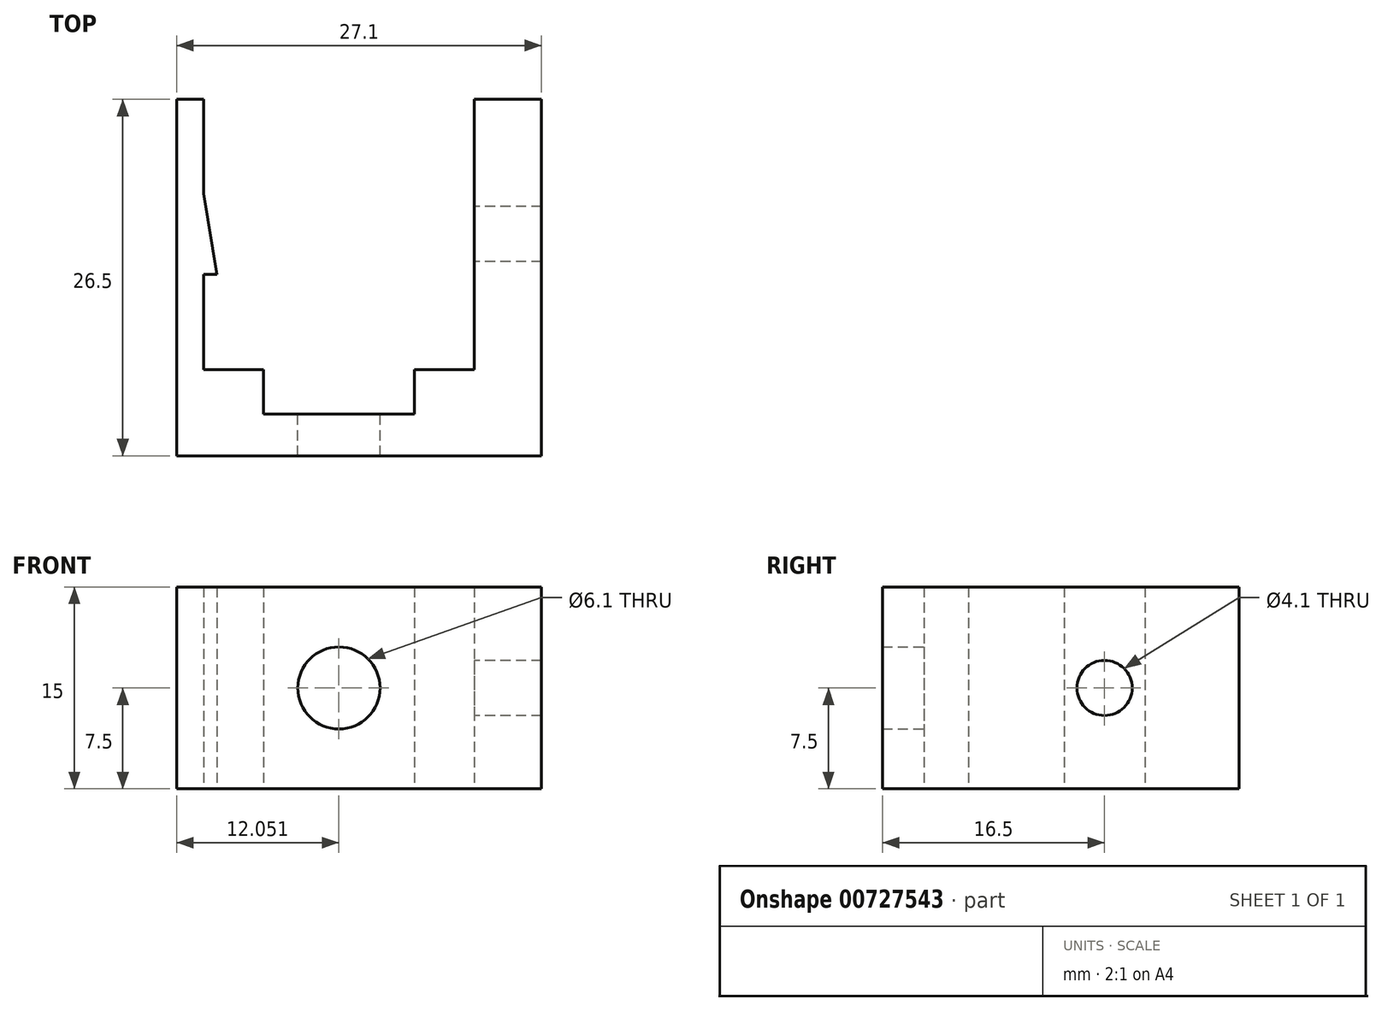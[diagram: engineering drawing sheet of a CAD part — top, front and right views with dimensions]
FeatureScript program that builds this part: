
annotation { "Feature Type Name" : "Feature", "Feature Type Description" : "" }
export const myFeature = defineFeature(function(context is Context, id is Id, definition is map)
    precondition{}
    {
        {
            var Q0;
            Q0=qCreatedBy(makeId("Top.planeOp"),FACE);
            var sketch = newSketch(context, id + "F0", { "sketchPlane" : qUnion([Q0])});
            skLineSegment(sketch, "E0", {"start": v(-10.68, 13) * mm, "end": v(-8.68, 13) * mm});
            skLineSegment(sketch, "E1", {"start": v(-8.68, 13) * mm, "end": v(-8.68, 6) * mm});
            skLineSegment(sketch, "E2", {"start": v(-8.68, 6) * mm, "end": v(-7.68, 0) * mm});
            skLineSegment(sketch, "E3", {"start": v(-7.68, 0) * mm, "end": v(-8.68, 0) * mm});
            skLineSegment(sketch, "E4", {"start": v(-8.68, 0) * mm, "end": v(-8.68, -7.1) * mm});
            skLineSegment(sketch, "E5", {"start": v(-8.68, -7.1) * mm, "end": v(-4.23, -7.1) * mm});
            skLineSegment(sketch, "E6", {"start": v(-4.23, -7.1) * mm, "end": v(-4.23, -10.4) * mm});
            skLineSegment(sketch, "E7", {"start": v(-4.23, -10.4) * mm, "end": v(6.97, -10.4) * mm});
            skLineSegment(sketch, "E8", {"start": v(6.97, -10.4) * mm, "end": v(6.97, -7.1) * mm});
            skLineSegment(sketch, "E9", {"start": v(6.97, -7.1) * mm, "end": v(11.42, -7.1) * mm});
            skLineSegment(sketch, "E10", {"start": v(11.42, 13) * mm, "end": v(16.42, 13) * mm});
            skLineSegment(sketch, "E11", {"start": v(16.42, 13) * mm, "end": v(16.42, -13.5) * mm});
            skLineSegment(sketch, "E12", {"start": v(16.42, -13.5) * mm, "end": v(-10.68, -13.5) * mm});
            skLineSegment(sketch, "E13", {"start": v(11.42, -7.1) * mm, "end": v(11.42, 13) * mm});
            skLineSegment(sketch, "E14", {"start": v(-10.68, 13) * mm, "end": v(-10.68, -13.5) * mm});
            skSolve(sketch);
        }
        {
            var Q0;
            Q0=makeQuery(id+"F0.imprint","IMPRINT",FACE,{"disambiguationData":[TD([[makeQuery(id+"F0.imprint","IMPRINT",EDGE,{"derivedFrom":sQuery(id+"F0.wireOp",EDGE,"E0")}),-1.0]])]});
            extrude(context, id + "F1", {"entities" : qUnion([Q0]), "depth" : 15 * mm, "offsetDistance" : 25 * mm});
        }
        {
            var Q0;
            Q0=makeQuery(id+"F1.opExtrude","SWEPT_FACE",FACE,{"disambiguationData":[OSD([sQuery(id+"F0.wireOp",EDGE,"E12")])]});
            var sketch = newSketch(context, id + "F2", { "sketchPlane" : qUnion([Q0])});
            skLineSegment(sketch, "E15", {"start": v(-4.23, 15) * mm, "end": v(6.97, 0) * mm, "construction": true});
            skPoint(sketch, "E16", {"position": v(1.37, 7.5) * mm});
            skLineSegment(sketch, "E17.0.0", {"start": v(6.97, 0) * mm, "end": v(-4.23, 0) * mm});
            skLineSegment(sketch, "E17.0.1", {"start": v(-4.23, 0) * mm, "end": v(-4.23, 15) * mm});
            skLineSegment(sketch, "E17.0.2", {"start": v(-4.23, 15) * mm, "end": v(6.97, 15) * mm});
            skLineSegment(sketch, "E17.0.3", {"start": v(6.97, 15) * mm, "end": v(6.97, 0) * mm});
            skSolve(sketch);
        }
        {
            var Q0;
            Q0=makeQuery(id+"F1.opExtrude","SWEPT_FACE",FACE,{"disambiguationData":[OSD([sQuery(id+"F0.wireOp",EDGE,"E11")])]});
            var sketch = newSketch(context, id + "F3", { "sketchPlane" : qUnion([Q0])});
            skLineSegment(sketch, "E18", {"start": v(13, 7.5) * mm, "end": v(-13.5, 7.5) * mm, "construction": true});
            skPoint(sketch, "E19", {"position": v(3, 7.5) * mm});
            skSolve(sketch);
        }
        {
            var Q0;
            Q0=sQuery(id+"F3.wireOp",VERTEX,"E19");
            var Q1;
            Q1=makeQuery(id+"F1.opExtrude","SWEPT_BODY",BODY,{"disambiguationData":[OSD([sQuery(id+"F0.wireOp",EDGE,"E0"),sQuery(id+"F0.wireOp",EDGE,"E1"),sQuery(id+"F0.wireOp",EDGE,"E2"),sQuery(id+"F0.wireOp",EDGE,"E3"),sQuery(id+"F0.wireOp",EDGE,"E4"),sQuery(id+"F0.wireOp",EDGE,"E5"),sQuery(id+"F0.wireOp",EDGE,"E6"),sQuery(id+"F0.wireOp",EDGE,"E7"),sQuery(id+"F0.wireOp",EDGE,"E8"),sQuery(id+"F0.wireOp",EDGE,"E9"),sQuery(id+"F0.wireOp",EDGE,"E10"),sQuery(id+"F0.wireOp",EDGE,"E11"),sQuery(id+"F0.wireOp",EDGE,"E12"),sQuery(id+"F0.wireOp",EDGE,"E13"),sQuery(id+"F0.wireOp",EDGE,"E14")])]});
            hole(context, id + "F4", {"style" : HoleStyle.SIMPLE, "endStyle" : HoleEndStyle.BLIND, "holeDiameter" : 4.1 * mm, "majorDiameter" : 20 * mm, "holeDepth" : 7 * mm, "tappedDepth" : 30 * mm, "tapClearance" : 3, "startFromSketch" : true, "locations" : qUnion([Q0]), "scope" : qUnion([Q1])});
        }
        {
            var Q0;
            Q0=sQuery(id+"F2.wireOp",VERTEX,"E16");
            var Q1;
            Q1=makeQuery(id+"F1.opExtrude","SWEPT_BODY",BODY,{"disambiguationData":[OSD([sQuery(id+"F0.wireOp",EDGE,"E0"),sQuery(id+"F0.wireOp",EDGE,"E1"),sQuery(id+"F0.wireOp",EDGE,"E2"),sQuery(id+"F0.wireOp",EDGE,"E3"),sQuery(id+"F0.wireOp",EDGE,"E4"),sQuery(id+"F0.wireOp",EDGE,"E5"),sQuery(id+"F0.wireOp",EDGE,"E6"),sQuery(id+"F0.wireOp",EDGE,"E7"),sQuery(id+"F0.wireOp",EDGE,"E8"),sQuery(id+"F0.wireOp",EDGE,"E9"),sQuery(id+"F0.wireOp",EDGE,"E10"),sQuery(id+"F0.wireOp",EDGE,"E11"),sQuery(id+"F0.wireOp",EDGE,"E12"),sQuery(id+"F0.wireOp",EDGE,"E13"),sQuery(id+"F0.wireOp",EDGE,"E14")])]});
            hole(context, id + "F5", {"style" : HoleStyle.SIMPLE, "endStyle" : HoleEndStyle.BLIND, "holeDiameter" : 6.1 * mm, "majorDiameter" : 5 * mm, "holeDepth" : 7 * mm, "tappedDepth" : 30 * mm, "tapClearance" : 3, "startFromSketch" : true, "locations" : qUnion([Q0]), "scope" : qUnion([Q1])});
        }
    });
